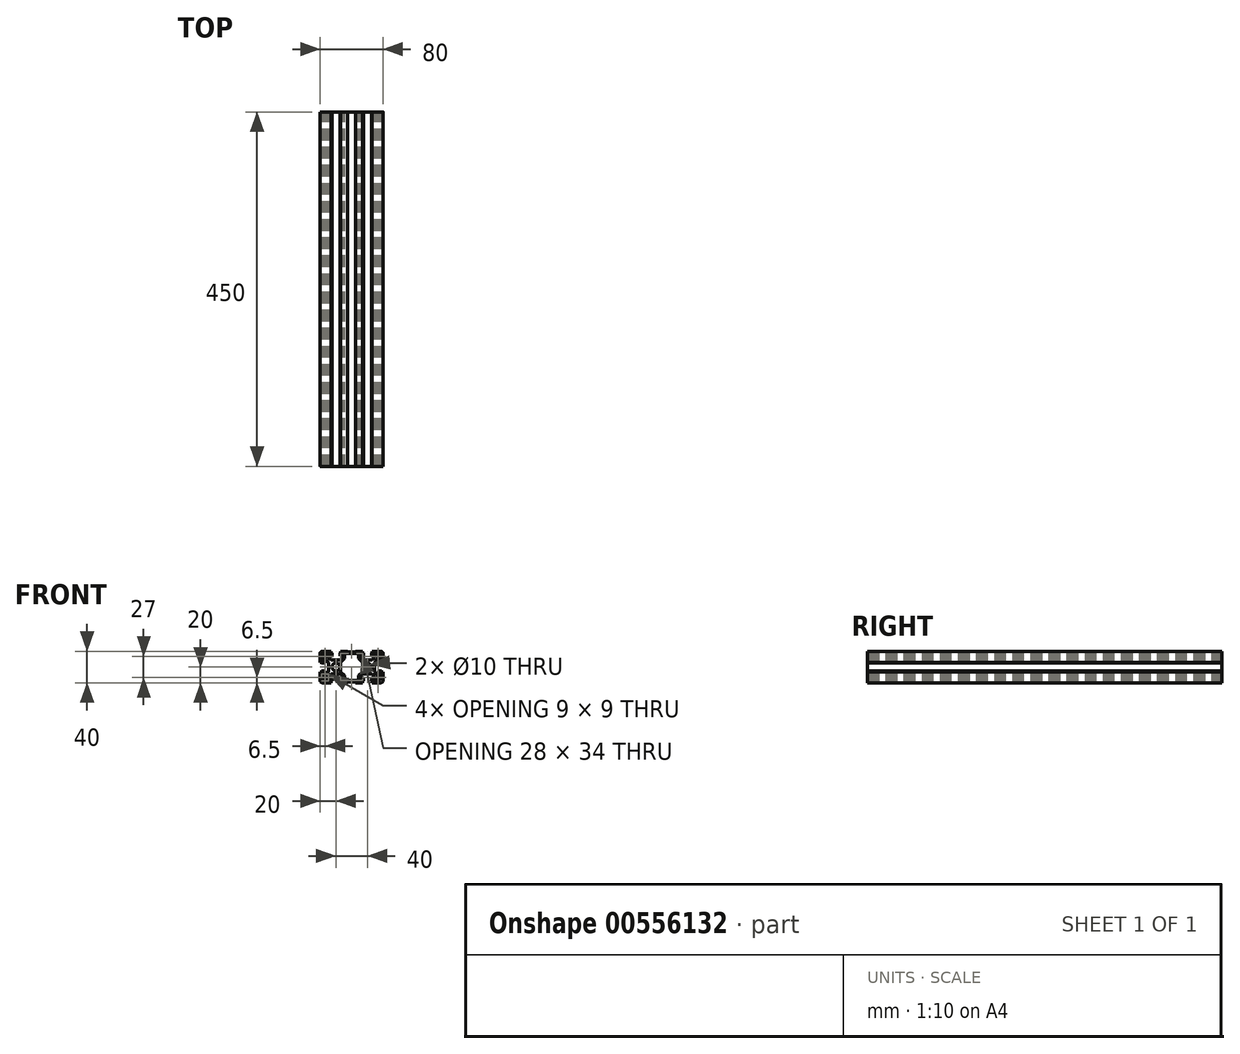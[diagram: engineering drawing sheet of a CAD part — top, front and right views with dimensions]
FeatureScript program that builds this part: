
annotation { "Feature Type Name" : "Feature", "Feature Type Description" : "" }
export const myFeature = defineFeature(function(context is Context, id is Id, definition is map)
    precondition{}
    {
        {
            assignVariable(context, id + "F0", {"name" : "Length", "anyValue" : 450});
        }
        {
            var Q0;
            Q0=qCreatedBy(makeId("Front.planeOp"),FACE);
            var sketch = newSketch(context, id + "F1", { "sketchPlane" : qUnion([Q0])});
            skLineSegment(sketch, "E0.bottom", {"start": v(40, 20) * mm, "end": v(-40, 20) * mm, "construction": true});
            skLineSegment(sketch, "E0.top", {"start": v(40, -20) * mm, "end": v(-40, -20) * mm, "construction": true});
            skLineSegment(sketch, "E0.left", {"start": v(40, 20) * mm, "end": v(40, -20) * mm, "construction": true});
            skLineSegment(sketch, "E0.right", {"start": v(-40, 20) * mm, "end": v(-40, -20) * mm, "construction": true});
            skPoint(sketch, "E0.middle", {"position": v(0, 0) * mm});
            skLineSegment(sketch, "E1", {"start": v(-38, 5) * mm, "end": v(-38, 6) * mm});
            skLineSegment(sketch, "E2", {"start": v(-38, 6) * mm, "end": v(-40, 6) * mm});
            skLineSegment(sketch, "E3", {"start": v(-40, 6) * mm, "end": v(-40, 17) * mm});
            skLineSegment(sketch, "E4", {"start": v(-38, 5) * mm, "end": v(-34, 5) * mm});
            skLineSegment(sketch, "E5", {"start": v(-34, 5) * mm, "end": v(-34, 9) * mm});
            skLineSegment(sketch, "E6", {"start": v(-29, 6) * mm, "end": v(-29, -6) * mm});
            skLineSegment(sketch, "E7", {"start": v(-34, -9) * mm, "end": v(-34, -5) * mm});
            skLineSegment(sketch, "E8", {"start": v(-34, -5) * mm, "end": v(-38, -5) * mm});
            skLineSegment(sketch, "E9", {"start": v(-38, -5) * mm, "end": v(-38, -6) * mm});
            skLineSegment(sketch, "E10", {"start": v(-38, -6) * mm, "end": v(-40, -6) * mm});
            skLineSegment(sketch, "E11", {"start": v(-40, -6) * mm, "end": v(-40, -17) * mm});
            skLineSegment(sketch, "E12", {"start": v(-34, -9) * mm, "end": v(-32, -9) * mm});
            skLineSegment(sketch, "E13", {"start": v(-32, -9) * mm, "end": v(-29, -6) * mm});
            skLineSegment(sketch, "E14", {"start": v(-29, 6) * mm, "end": v(-32, 9) * mm});
            skLineSegment(sketch, "E15", {"start": v(-32, 9) * mm, "end": v(-34, 9) * mm});
            skPoint(sketch, "E16", {"position": v(-29, 0) * mm});
            skLineSegment(sketch, "E17", {"start": v(-20, 0) * mm, "end": v(20, 0) * mm, "construction": true});
            skCircle(sketch, "E18", {"center": v(-20, 0) * mm, "radius": 5 * mm});
            skLineSegment(sketch, "E19", {"start": v(38, -5) * mm, "end": v(38, -6) * mm});
            skLineSegment(sketch, "E20", {"start": v(38, -6) * mm, "end": v(40, -6) * mm});
            skLineSegment(sketch, "E21", {"start": v(40, -6) * mm, "end": v(40, -17) * mm});
            skLineSegment(sketch, "E22", {"start": v(38, -5) * mm, "end": v(34, -5) * mm});
            skLineSegment(sketch, "E23", {"start": v(34, -5) * mm, "end": v(34, -9) * mm});
            skLineSegment(sketch, "E24", {"start": v(29, -6) * mm, "end": v(29, 6) * mm});
            skLineSegment(sketch, "E25", {"start": v(34, 9) * mm, "end": v(34, 5) * mm});
            skLineSegment(sketch, "E26", {"start": v(34, 5) * mm, "end": v(38, 5) * mm});
            skLineSegment(sketch, "E27", {"start": v(38, 5) * mm, "end": v(38, 6) * mm});
            skLineSegment(sketch, "E28", {"start": v(38, 6) * mm, "end": v(40, 6) * mm});
            skLineSegment(sketch, "E29", {"start": v(40, 6) * mm, "end": v(40, 17) * mm});
            skLineSegment(sketch, "E30", {"start": v(34, 9) * mm, "end": v(32, 9) * mm});
            skLineSegment(sketch, "E31", {"start": v(32, 9) * mm, "end": v(29, 6) * mm});
            skLineSegment(sketch, "E32", {"start": v(29, -6) * mm, "end": v(32, -9) * mm});
            skLineSegment(sketch, "E33", {"start": v(32, -9) * mm, "end": v(34, -9) * mm});
            skPoint(sketch, "E34", {"position": v(29, 0) * mm});
            skLineSegment(sketch, "E35", {"start": v(-15, 18) * mm, "end": v(-14, 18) * mm});
            skLineSegment(sketch, "E36", {"start": v(-14, 18) * mm, "end": v(-14, 20) * mm});
            skLineSegment(sketch, "E37", {"start": v(-14, 20) * mm, "end": v(-5, 20) * mm});
            skLineSegment(sketch, "E38", {"start": v(-15, 18) * mm, "end": v(-15, 14) * mm});
            skLineSegment(sketch, "E39", {"start": v(-15, 14) * mm, "end": v(-11, 14) * mm});
            skLineSegment(sketch, "E40", {"start": v(-14, 9) * mm, "end": v(-26, 9) * mm});
            skLineSegment(sketch, "E41", {"start": v(-29, 14) * mm, "end": v(-25, 14) * mm});
            skLineSegment(sketch, "E42", {"start": v(-25, 14) * mm, "end": v(-25, 18) * mm});
            skLineSegment(sketch, "E43", {"start": v(-25, 18) * mm, "end": v(-26, 18) * mm});
            skLineSegment(sketch, "E44", {"start": v(-26, 18) * mm, "end": v(-26, 20) * mm});
            skLineSegment(sketch, "E45", {"start": v(-26, 20) * mm, "end": v(-37, 20) * mm});
            skLineSegment(sketch, "E46", {"start": v(-29, 14) * mm, "end": v(-29, 12) * mm});
            skLineSegment(sketch, "E47", {"start": v(-29, 12) * mm, "end": v(-26, 9) * mm});
            skLineSegment(sketch, "E48", {"start": v(-14, 9) * mm, "end": v(-11, 12) * mm});
            skLineSegment(sketch, "E49", {"start": v(-11, 12) * mm, "end": v(-11, 14) * mm});
            skPoint(sketch, "E50", {"position": v(-20, 9) * mm});
            skLineSegment(sketch, "E51", {"start": v(25, 18) * mm, "end": v(26, 18) * mm});
            skLineSegment(sketch, "E52", {"start": v(26, 18) * mm, "end": v(26, 20) * mm});
            skLineSegment(sketch, "E53", {"start": v(26, 20) * mm, "end": v(37, 20) * mm});
            skLineSegment(sketch, "E54", {"start": v(25, 18) * mm, "end": v(25, 14) * mm});
            skLineSegment(sketch, "E55", {"start": v(25, 14) * mm, "end": v(29, 14) * mm});
            skLineSegment(sketch, "E56", {"start": v(26, 9) * mm, "end": v(14, 9) * mm});
            skLineSegment(sketch, "E57", {"start": v(11, 14) * mm, "end": v(15, 14) * mm});
            skLineSegment(sketch, "E58", {"start": v(15, 14) * mm, "end": v(15, 18) * mm});
            skLineSegment(sketch, "E59", {"start": v(15, 18) * mm, "end": v(14, 18) * mm});
            skLineSegment(sketch, "E60", {"start": v(14, 18) * mm, "end": v(14, 20) * mm});
            skLineSegment(sketch, "E61", {"start": v(14, 20) * mm, "end": v(5, 20) * mm});
            skLineSegment(sketch, "E62", {"start": v(11, 14) * mm, "end": v(11, 12) * mm});
            skLineSegment(sketch, "E63", {"start": v(11, 12) * mm, "end": v(14, 9) * mm});
            skLineSegment(sketch, "E64", {"start": v(26, 9) * mm, "end": v(29, 12) * mm});
            skLineSegment(sketch, "E65", {"start": v(29, 12) * mm, "end": v(29, 14) * mm});
            skPoint(sketch, "E66", {"position": v(20, 9) * mm});
            skLineSegment(sketch, "E67", {"start": v(-25, -18) * mm, "end": v(-26, -18) * mm});
            skLineSegment(sketch, "E68", {"start": v(-26, -18) * mm, "end": v(-26, -20) * mm});
            skLineSegment(sketch, "E69", {"start": v(-26, -20) * mm, "end": v(-37, -20) * mm});
            skLineSegment(sketch, "E70", {"start": v(-25, -18) * mm, "end": v(-25, -14) * mm});
            skLineSegment(sketch, "E71", {"start": v(-25, -14) * mm, "end": v(-29, -14) * mm});
            skLineSegment(sketch, "E72", {"start": v(-26, -9) * mm, "end": v(-14, -9) * mm});
            skLineSegment(sketch, "E73", {"start": v(-11, -14) * mm, "end": v(-15, -14) * mm});
            skLineSegment(sketch, "E74", {"start": v(-15, -14) * mm, "end": v(-15, -18) * mm});
            skLineSegment(sketch, "E75", {"start": v(-15, -18) * mm, "end": v(-14, -18) * mm});
            skLineSegment(sketch, "E76", {"start": v(-14, -18) * mm, "end": v(-14, -20) * mm});
            skLineSegment(sketch, "E77", {"start": v(-5, -20) * mm, "end": v(-14, -20) * mm});
            skLineSegment(sketch, "E78", {"start": v(-11, -14) * mm, "end": v(-11, -12) * mm});
            skLineSegment(sketch, "E79", {"start": v(-11, -12) * mm, "end": v(-14, -9) * mm});
            skLineSegment(sketch, "E80", {"start": v(-26, -9) * mm, "end": v(-29, -12) * mm});
            skLineSegment(sketch, "E81", {"start": v(-29, -12) * mm, "end": v(-29, -14) * mm});
            skPoint(sketch, "E82", {"position": v(-20, -9) * mm});
            skLineSegment(sketch, "E83", {"start": v(15, -18) * mm, "end": v(14, -18) * mm});
            skLineSegment(sketch, "E84", {"start": v(14, -18) * mm, "end": v(14, -20) * mm});
            skLineSegment(sketch, "E85", {"start": v(14, -20) * mm, "end": v(5, -20) * mm});
            skLineSegment(sketch, "E86", {"start": v(15, -18) * mm, "end": v(15, -14) * mm});
            skLineSegment(sketch, "E87", {"start": v(15, -14) * mm, "end": v(11, -14) * mm});
            skLineSegment(sketch, "E88", {"start": v(14, -9) * mm, "end": v(26, -9) * mm});
            skLineSegment(sketch, "E89", {"start": v(29, -14) * mm, "end": v(25, -14) * mm});
            skLineSegment(sketch, "E90", {"start": v(25, -14) * mm, "end": v(25, -18) * mm});
            skLineSegment(sketch, "E91", {"start": v(25, -18) * mm, "end": v(26, -18) * mm});
            skLineSegment(sketch, "E92", {"start": v(26, -18) * mm, "end": v(26, -20) * mm});
            skLineSegment(sketch, "E93", {"start": v(26, -20) * mm, "end": v(37, -20) * mm});
            skLineSegment(sketch, "E94", {"start": v(29, -14) * mm, "end": v(29, -12) * mm});
            skLineSegment(sketch, "E95", {"start": v(29, -12) * mm, "end": v(26, -9) * mm});
            skLineSegment(sketch, "E96", {"start": v(14, -9) * mm, "end": v(11, -12) * mm});
            skLineSegment(sketch, "E97", {"start": v(11, -12) * mm, "end": v(11, -14) * mm});
            skPoint(sketch, "E98", {"position": v(20, -9) * mm});
            skLineSegment(sketch, "E99", {"start": v(-20, -20) * mm, "end": v(-20, 20) * mm, "construction": true});
            skLineSegment(sketch, "E100", {"start": v(20, 20) * mm, "end": v(20, -20) * mm, "construction": true});
            skLineSegment(sketch, "E101", {"start": v(-5, -20) * mm, "end": v(-5, -19) * mm});
            skLineSegment(sketch, "E102", {"start": v(-5, -19) * mm, "end": v(5, -19) * mm});
            skLineSegment(sketch, "E103", {"start": v(5, -19) * mm, "end": v(5, -20) * mm});
            skPoint(sketch, "E104", {"position": v(0, -19) * mm});
            skLineSegment(sketch, "E105", {"start": v(-5, 20) * mm, "end": v(-5, 19) * mm});
            skLineSegment(sketch, "E106", {"start": v(-5, 19) * mm, "end": v(5, 19) * mm});
            skLineSegment(sketch, "E107", {"start": v(5, 19) * mm, "end": v(5, 20) * mm});
            skPoint(sketch, "E108", {"position": v(0, 19) * mm});
            skArc(sketch, "E109", {"start": v(-37, 20) * mm, "mid": v(-39.12, 19.12) * mm, "end": v(-40, 17) * mm});
            skArc(sketch, "E110", {"start": v(-40, -17) * mm, "mid": v(-39.12, -19.12) * mm, "end": v(-37, -20) * mm});
            skArc(sketch, "E111", {"start": v(37, -20) * mm, "mid": v(39.12, -19.12) * mm, "end": v(40, -17) * mm});
            skArc(sketch, "E112", {"start": v(40, 17) * mm, "mid": v(39.12, 19.12) * mm, "end": v(37, 20) * mm});
            skLineSegment(sketch, "E113", {"start": v(-40, 17) * mm, "end": v(-40, 20) * mm, "construction": true});
            skLineSegment(sketch, "E114.bottom", {"start": v(-40, 20) * mm, "end": v(-37, 20) * mm, "construction": true});
            skLineSegment(sketch, "E114.top", {"start": v(-40, 17) * mm, "end": v(-37, 17) * mm, "construction": true});
            skLineSegment(sketch, "E114.left", {"start": v(-40, 20) * mm, "end": v(-40, 17) * mm, "construction": true});
            skLineSegment(sketch, "E114.right", {"start": v(-37, 20) * mm, "end": v(-37, 17) * mm, "construction": true});
            skLineSegment(sketch, "E115.bottom", {"start": v(-40, -20) * mm, "end": v(-37, -20) * mm, "construction": true});
            skLineSegment(sketch, "E115.top", {"start": v(-40, -17) * mm, "end": v(-37, -17) * mm, "construction": true});
            skLineSegment(sketch, "E115.left", {"start": v(-40, -20) * mm, "end": v(-40, -17) * mm, "construction": true});
            skLineSegment(sketch, "E115.right", {"start": v(-37, -20) * mm, "end": v(-37, -17) * mm, "construction": true});
            skLineSegment(sketch, "E116.bottom", {"start": v(40, -20) * mm, "end": v(37, -20) * mm, "construction": true});
            skLineSegment(sketch, "E116.top", {"start": v(40, -17) * mm, "end": v(37, -17) * mm, "construction": true});
            skLineSegment(sketch, "E116.left", {"start": v(40, -20) * mm, "end": v(40, -17) * mm, "construction": true});
            skLineSegment(sketch, "E116.right", {"start": v(37, -20) * mm, "end": v(37, -17) * mm, "construction": true});
            skLineSegment(sketch, "E117.bottom", {"start": v(40, 20) * mm, "end": v(37, 20) * mm, "construction": true});
            skLineSegment(sketch, "E117.top", {"start": v(40, 17) * mm, "end": v(37, 17) * mm, "construction": true});
            skLineSegment(sketch, "E117.left", {"start": v(40, 20) * mm, "end": v(40, 17) * mm, "construction": true});
            skLineSegment(sketch, "E117.right", {"start": v(37, 20) * mm, "end": v(37, 17) * mm, "construction": true});
            skCircle(sketch, "E118", {"center": v(20, 0) * mm, "radius": 5 * mm});
            skLineSegment(sketch, "E119", {"start": v(-9, -17) * mm, "end": v(9, -17) * mm});
            skLineSegment(sketch, "E120", {"start": v(9, -17) * mm, "end": v(9, -11) * mm});
            skLineSegment(sketch, "E121", {"start": v(9, -11) * mm, "end": v(14, -6) * mm});
            skLineSegment(sketch, "E122", {"start": v(14, -6) * mm, "end": v(14, 6) * mm});
            skLineSegment(sketch, "E123", {"start": v(14, 6) * mm, "end": v(9, 11) * mm});
            skLineSegment(sketch, "E124", {"start": v(9, 11) * mm, "end": v(9, 17) * mm});
            skLineSegment(sketch, "E125", {"start": v(9, 17) * mm, "end": v(-9, 17) * mm});
            skLineSegment(sketch, "E126", {"start": v(-9, 17) * mm, "end": v(-9, 11) * mm});
            skLineSegment(sketch, "E127", {"start": v(-9, 11) * mm, "end": v(-14, 6) * mm});
            skLineSegment(sketch, "E128", {"start": v(-14, 6) * mm, "end": v(-14, -6) * mm});
            skLineSegment(sketch, "E129", {"start": v(-14, -6) * mm, "end": v(-9, -11) * mm});
            skLineSegment(sketch, "E130", {"start": v(-9, -11) * mm, "end": v(-9, -17) * mm});
            skPoint(sketch, "E131", {"position": v(0, 17) * mm});
            skArc(sketch, "E132", {"start": v(-38, 10) * mm, "mid": v(-37, 9) * mm, "end": v(-36, 10) * mm});
            skArc(sketch, "E133", {"start": v(-30, 16) * mm, "mid": v(-29, 17) * mm, "end": v(-30, 18) * mm});
            skLineSegment(sketch, "E134", {"start": v(-30, 18) * mm, "end": v(-34, 18) * mm});
            skLineSegment(sketch, "E135", {"start": v(-34, 18) * mm, "end": v(-34, 17) * mm});
            skLineSegment(sketch, "E136", {"start": v(-38, 10) * mm, "end": v(-38, 14) * mm});
            skLineSegment(sketch, "E137", {"start": v(-38, 14) * mm, "end": v(-37, 14) * mm});
            skArc(sketch, "E138", {"start": v(-34, 17) * mm, "mid": v(-36.12, 16.12) * mm, "end": v(-37, 14) * mm});
            skLineSegment(sketch, "E139", {"start": v(-36, 10) * mm, "end": v(-36, 11) * mm});
            skLineSegment(sketch, "E140", {"start": v(-36, 11) * mm, "end": v(-34, 11) * mm});
            skLineSegment(sketch, "E141", {"start": v(-30, 16) * mm, "end": v(-31, 16) * mm});
            skLineSegment(sketch, "E142", {"start": v(-31, 16) * mm, "end": v(-31, 14) * mm});
            skArc(sketch, "E143", {"start": v(-34, 11) * mm, "mid": v(-31.88, 11.88) * mm, "end": v(-31, 14) * mm});
            skArc(sketch, "E144", {"start": v(30, 18) * mm, "mid": v(29, 17) * mm, "end": v(30, 16) * mm});
            skArc(sketch, "E145", {"start": v(36, 10) * mm, "mid": v(37, 9) * mm, "end": v(38, 10) * mm});
            skLineSegment(sketch, "E146", {"start": v(38, 10) * mm, "end": v(38, 14) * mm});
            skLineSegment(sketch, "E147", {"start": v(38, 14) * mm, "end": v(37, 14) * mm});
            skLineSegment(sketch, "E148", {"start": v(30, 18) * mm, "end": v(34, 18) * mm});
            skLineSegment(sketch, "E149", {"start": v(34, 18) * mm, "end": v(34, 17) * mm});
            skArc(sketch, "E150", {"start": v(37, 14) * mm, "mid": v(36.12, 16.12) * mm, "end": v(34, 17) * mm});
            skLineSegment(sketch, "E151", {"start": v(30, 16) * mm, "end": v(31, 16) * mm});
            skLineSegment(sketch, "E152", {"start": v(31, 16) * mm, "end": v(31, 14) * mm});
            skLineSegment(sketch, "E153", {"start": v(36, 10) * mm, "end": v(36, 11) * mm});
            skLineSegment(sketch, "E154", {"start": v(36, 11) * mm, "end": v(34, 11) * mm});
            skArc(sketch, "E155", {"start": v(31, 14) * mm, "mid": v(31.88, 11.88) * mm, "end": v(34, 11) * mm});
            skArc(sketch, "E156", {"start": v(38, -10) * mm, "mid": v(37, -9) * mm, "end": v(36, -10) * mm});
            skArc(sketch, "E157", {"start": v(30, -16) * mm, "mid": v(29, -17) * mm, "end": v(30, -18) * mm});
            skLineSegment(sketch, "E158", {"start": v(30, -18) * mm, "end": v(34, -18) * mm});
            skLineSegment(sketch, "E159", {"start": v(34, -18) * mm, "end": v(34, -17) * mm});
            skLineSegment(sketch, "E160", {"start": v(38, -10) * mm, "end": v(38, -14) * mm});
            skLineSegment(sketch, "E161", {"start": v(38, -14) * mm, "end": v(37, -14) * mm});
            skArc(sketch, "E162", {"start": v(34, -17) * mm, "mid": v(36.12, -16.12) * mm, "end": v(37, -14) * mm});
            skLineSegment(sketch, "E163", {"start": v(36, -10) * mm, "end": v(36, -11) * mm});
            skLineSegment(sketch, "E164", {"start": v(36, -11) * mm, "end": v(34, -11) * mm});
            skLineSegment(sketch, "E165", {"start": v(30, -16) * mm, "end": v(31, -16) * mm});
            skLineSegment(sketch, "E166", {"start": v(31, -16) * mm, "end": v(31, -14) * mm});
            skArc(sketch, "E167", {"start": v(34, -11) * mm, "mid": v(31.88, -11.88) * mm, "end": v(31, -14) * mm});
            skArc(sketch, "E168", {"start": v(-30, -18) * mm, "mid": v(-29, -17) * mm, "end": v(-30, -16) * mm});
            skArc(sketch, "E169", {"start": v(-36, -10) * mm, "mid": v(-37, -9) * mm, "end": v(-38, -10) * mm});
            skLineSegment(sketch, "E170", {"start": v(-38, -10) * mm, "end": v(-38, -14) * mm});
            skLineSegment(sketch, "E171", {"start": v(-38, -14) * mm, "end": v(-37, -14) * mm});
            skLineSegment(sketch, "E172", {"start": v(-30, -18) * mm, "end": v(-34, -18) * mm});
            skLineSegment(sketch, "E173", {"start": v(-34, -18) * mm, "end": v(-34, -17) * mm});
            skArc(sketch, "E174", {"start": v(-37, -14) * mm, "mid": v(-36.12, -16.12) * mm, "end": v(-34, -17) * mm});
            skLineSegment(sketch, "E175", {"start": v(-30, -16) * mm, "end": v(-31, -16) * mm});
            skLineSegment(sketch, "E176", {"start": v(-31, -16) * mm, "end": v(-31, -14) * mm});
            skLineSegment(sketch, "E177", {"start": v(-36, -10) * mm, "end": v(-36, -11) * mm});
            skLineSegment(sketch, "E178", {"start": v(-36, -11) * mm, "end": v(-34, -11) * mm});
            skArc(sketch, "E179", {"start": v(-31, -14) * mm, "mid": v(-31.88, -11.88) * mm, "end": v(-34, -11) * mm});
            skSolve(sketch);
        }
        {
            var Q0;
            Q0=makeQuery(id+"F1.imprint","IMPRINT",FACE,{"disambiguationData":[TD([[makeQuery(id+"F1.imprint","IMPRINT",EDGE,{"derivedFrom":sQuery(id+"F1.wireOp",EDGE,"E1")}),-1.0]])]});
            extrude(context, id + "F2", {"entities" : qUnion([Q0]), "depth" : (getVariable(context, 'Length')) * mm, "offsetDistance" : 25 * mm});
        }
    });
